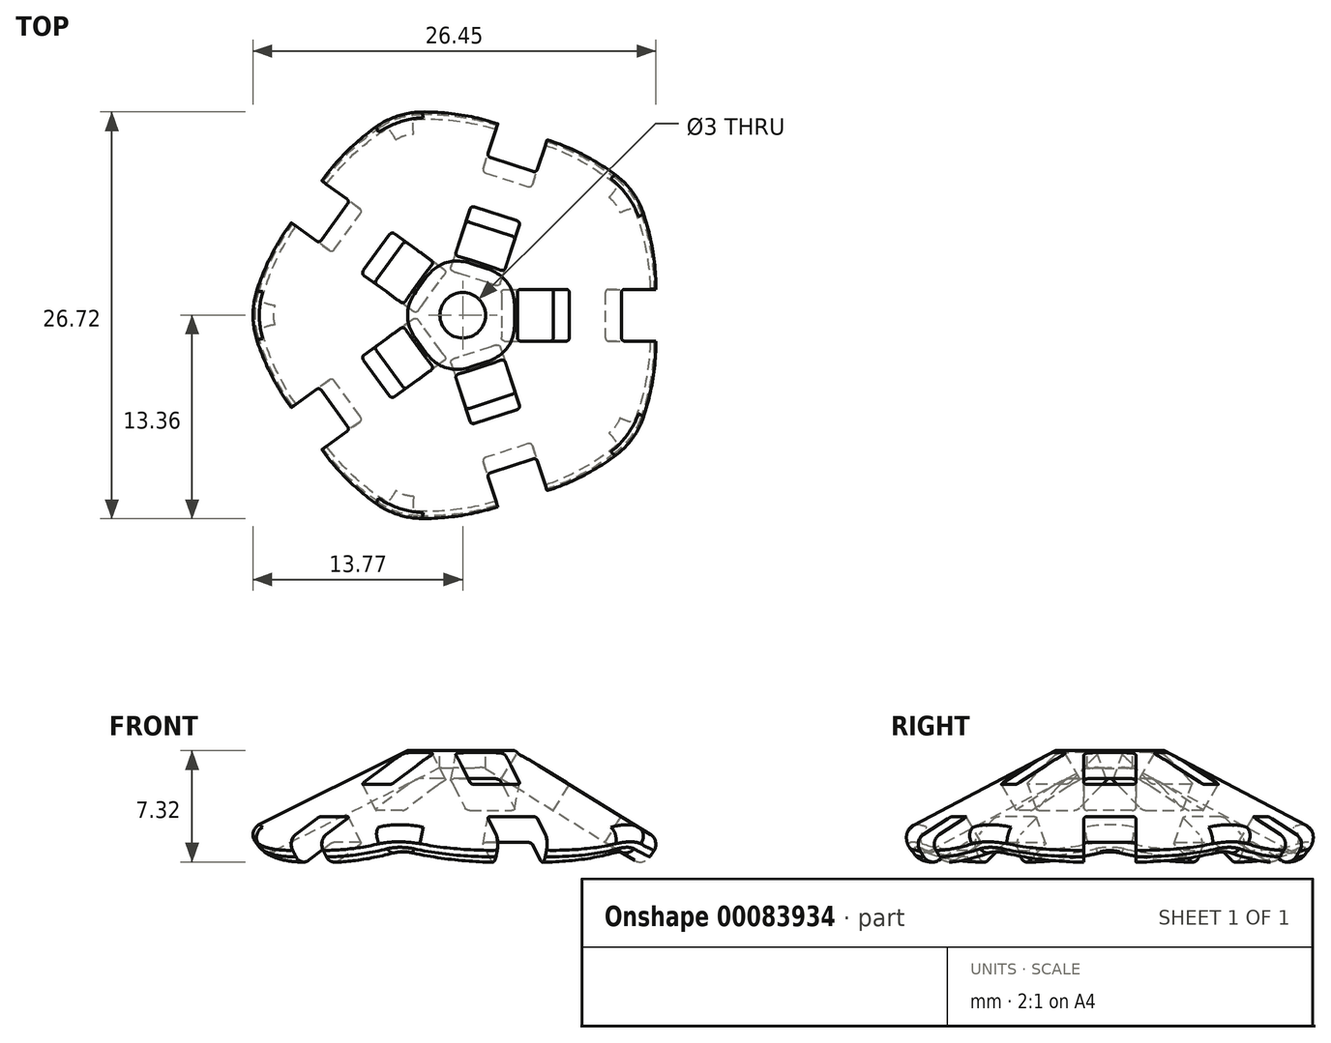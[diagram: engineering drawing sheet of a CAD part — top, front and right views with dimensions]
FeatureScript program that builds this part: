
annotation { "Feature Type Name" : "Feature", "Feature Type Description" : "" }
export const myFeature = defineFeature(function(context is Context, id is Id, definition is map)
    precondition{}
    {
        {
            var Q0;
            Q0=qCreatedBy(makeId("Front.planeOp"),FACE);
            var sketch = newSketch(context, id + "F0", { "sketchPlane" : qUnion([Q0])});
            skLineSegment(sketch, "E0", {"start": v(0, 0) * mm, "end": v(11.9, -7.36) * mm});
            skLineSegment(sketch, "E1.0", {"start": v(1.05, 1.7) * mm, "end": v(12.96, -5.66) * mm});
            skLineSegment(sketch, "E2", {"start": v(1.05, 1.7) * mm, "end": v(0, 0) * mm});
            skLineSegment(sketch, "E3", {"start": v(12.96, -5.66) * mm, "end": v(11.9, -7.36) * mm});
            skLineSegment(sketch, "E4", {"start": v(0, 0) * mm, "end": v(0, -18.92) * mm, "construction": true});
            skSolve(sketch);
        }
        {
            var Q0;
            Q0 = qSketchRegion(id + "F0", true);
            extrude(context, id + "F1", {"entities" : qUnion([Q0]), "endBound" : BoundingType.SYMMETRIC, "depth" : 20 * mm});
        }
        {
            var Q0;
            Q0=qCreatedBy(makeId("Top.planeOp"),FACE);
            var sketch = newSketch(context, id + "F2", { "sketchPlane" : qUnion([Q0])});
            skLineSegment(sketch, "E5", {"start": v(0, 0) * mm, "end": v(17.2, -12.5) * mm});
            skLineSegment(sketch, "E6", {"start": v(0, 0) * mm, "end": v(17.2, 12.5) * mm});
            skLineSegment(sketch, "E7", {"start": v(17.2, -12.5) * mm, "end": v(-2, -12.5) * mm});
            skLineSegment(sketch, "E8", {"start": v(-2, -12.5) * mm, "end": v(-2, 12.5) * mm});
            skLineSegment(sketch, "E9", {"start": v(-2, 12.5) * mm, "end": v(17.2, 12.5) * mm});
            skLineSegment(sketch, "E10", {"start": v(0, 0) * mm, "end": v(-2, 0) * mm});
            skLineSegment(sketch, "E11", {"start": v(17.2, -12.5) * mm, "end": v(17.2, 12.5) * mm});
            skSolve(sketch);
        }
        {
            var Q0;
            Q0=makeQuery(id+"F2.imprint","IMPRINT",FACE,{"disambiguationData":[TD([[makeQuery(id+"F2.imprint","IMPRINT",EDGE,{"derivedFrom":sQuery(id+"F2.wireOp",EDGE,"E6")}),1.0]])]});
            var Q1;
            Q1=makeQuery(id+"F2.imprint","IMPRINT",FACE,{"disambiguationData":[TD([[makeQuery(id+"F2.imprint","IMPRINT",EDGE,{"derivedFrom":sQuery(id+"F2.wireOp",EDGE,"E5")}),-1.0]])]});
            extrude(context, id + "F3", {"entities" : qUnion([Q0, Q1]), "operationType" : NewBodyOperationType.REMOVE, "endBound" : BoundingType.SYMMETRIC, "oppositeDirection" : true, "depth" : 25 * mm});
        }
        {
            var Q0;
            Q0=makeQuery(id+"F1.opExtrude","SWEPT_FACE",FACE,{"disambiguationData":[OSD([sQuery(id+"F0.wireOp",EDGE,"E1.0")])]});
            var sketch = newSketch(context, id + "F4", { "sketchPlane" : qUnion([Q0])});
            skLineSegment(sketch, "E12", {"start": v(0, 0) * mm, "end": v(14, 0) * mm, "construction": true});
            skLineSegment(sketch, "E13.bottom", {"start": v(11.25, -1.7) * mm, "end": v(15, -1.7) * mm});
            skLineSegment(sketch, "E13.top", {"start": v(11.25, 1.7) * mm, "end": v(15, 1.7) * mm});
            skLineSegment(sketch, "E13.left", {"start": v(11, -1.45) * mm, "end": v(11, 1.45) * mm});
            skPoint(sketch, "E13.middle", {"position": v(13, 0) * mm});
            skLineSegment(sketch, "E14.bottom", {"start": v(6.75, -1.7) * mm, "end": v(3.25, -1.7) * mm});
            skLineSegment(sketch, "E14.top", {"start": v(6.75, 1.7) * mm, "end": v(3.25, 1.7) * mm});
            skLineSegment(sketch, "E14.left", {"start": v(7, -1.45) * mm, "end": v(7, 1.45) * mm});
            skLineSegment(sketch, "E14.right", {"start": v(3, -1.45) * mm, "end": v(3, 1.45) * mm});
            skPoint(sketch, "E14.middle", {"position": v(5, 0) * mm});
            skPoint(sketch, "E15.visualSharp", {"position": v(3, -1.7) * mm});
            skArc(sketch, "E15.filletArc", {"start": v(3, -1.45) * mm, "mid": v(3.07, -1.63) * mm, "end": v(3.25, -1.7) * mm});
            skPoint(sketch, "E16.visualSharp", {"position": v(3, 1.7) * mm});
            skArc(sketch, "E16.filletArc", {"start": v(3.25, 1.7) * mm, "mid": v(3.07, 1.63) * mm, "end": v(3, 1.45) * mm});
            skPoint(sketch, "E17.visualSharp", {"position": v(7, -1.7) * mm});
            skArc(sketch, "E17.filletArc", {"start": v(6.75, -1.7) * mm, "mid": v(6.93, -1.63) * mm, "end": v(7, -1.45) * mm});
            skPoint(sketch, "E18.visualSharp", {"position": v(7, 1.7) * mm});
            skArc(sketch, "E18.filletArc", {"start": v(7, 1.45) * mm, "mid": v(6.93, 1.63) * mm, "end": v(6.75, 1.7) * mm});
            skPoint(sketch, "E19.visualSharp", {"position": v(11, 1.7) * mm});
            skArc(sketch, "E19.filletArc", {"start": v(11.25, 1.7) * mm, "mid": v(11.07, 1.63) * mm, "end": v(11, 1.45) * mm});
            skPoint(sketch, "E20.visualSharp", {"position": v(15, 1.7) * mm});
            skPoint(sketch, "E21.visualSharp", {"position": v(11, -1.7) * mm});
            skArc(sketch, "E21.filletArc", {"start": v(11, -1.45) * mm, "mid": v(11.07, -1.63) * mm, "end": v(11.25, -1.7) * mm});
            skPoint(sketch, "E22.visualSharp", {"position": v(15, -1.7) * mm});
            skLineSegment(sketch, "E23", {"start": v(15, -1.7) * mm, "end": v(15, 1.7) * mm});
            skSolve(sketch);
        }
        {
            var Q0;
            {var subQ0=sQuery(id+"F4.wireOp",EDGE,"E23");Q0=makeQuery(id+"F4.imprint","IMPRINT",FACE,{"disambiguationData":[TD([[makeQuery(id+"F4.imprint","IMPRINT",EDGE,{"derivedFrom":subQ0}),1.0]])]});}
            var Q1;
            Q1=makeQuery(id+"F4.imprint","IMPRINT",FACE,{"disambiguationData":[TD([[makeQuery(id+"F4.imprint","IMPRINT",EDGE,{"derivedFrom":sQuery(id+"F4.wireOp",EDGE,"E13.left")}),-1.0]])]});
            var Q2;
            {var subQ0=sQuery(id+"F4.wireOp",EDGE,"E23");Q2=makeQuery(id+"F4.imprint","IMPRINT",FACE,{"disambiguationData":[TD([[makeQuery(id+"F4.imprint","IMPRINT",EDGE,{"derivedFrom":subQ0}),1.0]])]});}
            var Q3;
            Q3=makeQuery(id+"F4.imprint","IMPRINT",FACE,{"disambiguationData":[TD([[makeQuery(id+"F4.imprint","IMPRINT",EDGE,{"derivedFrom":sQuery(id+"F4.wireOp",EDGE,"E14.bottom")}),-1.0]])]});
            extrude(context, id + "F5", {"entities" : qUnion([Q0, Q1, Q2, Q3]), "operationType" : NewBodyOperationType.REMOVE, "endBound" : BoundingType.UP_TO_NEXT, "oppositeDirection" : true, "depth" : 25 * mm});
        }
        {
            var Q0;
            Q0=qCreatedBy(makeId("Top.planeOp"),FACE);
            var sketch = newSketch(context, id + "F6", { "sketchPlane" : qUnion([Q0])});
            skCircle(sketch, "E24", {"center": v(0, 0) * mm, "radius": 2 * mm});
            skSolve(sketch);
        }
        {
            var Q0;
            Q0 = qSketchRegion(id + "F6", true);
            extrude(context, id + "F7", {"entities" : qUnion([Q0]), "operationType" : NewBodyOperationType.ADD, "depth" : 1.75 * mm});
        }
        {
            var Q0;
            Q0=makeQuery(id+"F1.opExtrude","SWEPT_BODY",BODY,{"disambiguationData":[OSD([sQuery(id+"F0.wireOp",EDGE,"E0"),sQuery(id+"F0.wireOp",EDGE,"E1.0"),sQuery(id+"F0.wireOp",EDGE,"E2"),sQuery(id+"F0.wireOp",EDGE,"E3")])]});
            var Q1;
            Q1=sQuery(id+"F0.wireOp",EDGE,"E4");
            circularPattern(context, id + "F8", {"operationType" : NewBodyOperationType.ADD, "entities" : qUnion([Q0]), "axis" : qUnion([Q1]), "angle" : 360 * degree, "instanceCount" : 5, "equalSpace" : true});
        }
        {
            var Q0;
            Q0=makeQuery(id+"F7.opExtrude","CAP_FACE",FACE,{"disambiguationData":[OSD([sQuery(id+"F6.wireOp",EDGE,"E24")])],"isStart":false});
            var sketch = newSketch(context, id + "F9", { "sketchPlane" : qUnion([Q0])});
            skCircle(sketch, "E25", {"center": v(0, 0) * mm, "radius": 1.5 * mm});
            skSolve(sketch);
        }
        {
            var Q0;
            Q0 = qSketchRegion(id + "F9", true);
            extrude(context, id + "F10", {"entities" : qUnion([Q0]), "operationType" : NewBodyOperationType.REMOVE, "oppositeDirection" : true, "depth" : 25 * mm});
        }
        {
            var Q0;
            {var subQ0=makeQuery(id+"F1.opExtrude","SWEPT_FACE",FACE,{"disambiguationData":[OSD([sQuery(id+"F0.wireOp",EDGE,"E1.0")])]});Q0=makeQuery(id+"F8.boolean.opBoolean","MERGE",EDGE,{"derivedFrom":[makeQuery(id+"F8.opPattern","COPY",EDGE,{"derivedFrom":makeQuery(id+"F3.boolean.opBoolean","INTERSECT",EDGE,{"derivedFrom":[subQ0,makeQuery(id+"F3.opExtrude","SWEPT_FACE",FACE,{"disambiguationData":[OSD([sQuery(id+"F2.wireOp",EDGE,"E5")])]})]}),"instanceName":"1"}),makeQuery(id+"F8.opPattern","COPY",EDGE,{"derivedFrom":makeQuery(id+"F3.boolean.opBoolean","INTERSECT",EDGE,{"derivedFrom":[subQ0,makeQuery(id+"F3.opExtrude","SWEPT_FACE",FACE,{"disambiguationData":[OSD([sQuery(id+"F2.wireOp",EDGE,"E6")])]})]}),"instanceName":"2"})]});}
            var Q1;
            {var subQ0=makeQuery(id+"F1.opExtrude","SWEPT_FACE",FACE,{"disambiguationData":[OSD([sQuery(id+"F0.wireOp",EDGE,"E1.0")])]});Q1=makeQuery(id+"F8.boolean.opBoolean","MERGE",EDGE,{"derivedFrom":[makeQuery(id+"F3.boolean.opBoolean","INTERSECT",EDGE,{"derivedFrom":[subQ0,makeQuery(id+"F3.opExtrude","SWEPT_FACE",FACE,{"disambiguationData":[OSD([sQuery(id+"F2.wireOp",EDGE,"E5")])]})]}),makeQuery(id+"F8.opPattern","COPY",EDGE,{"derivedFrom":makeQuery(id+"F3.boolean.opBoolean","INTERSECT",EDGE,{"derivedFrom":[subQ0,makeQuery(id+"F3.opExtrude","SWEPT_FACE",FACE,{"disambiguationData":[OSD([sQuery(id+"F2.wireOp",EDGE,"E6")])]})]}),"instanceName":"1"})]});}
            var Q2;
            {var subQ0=makeQuery(id+"F1.opExtrude","SWEPT_FACE",FACE,{"disambiguationData":[OSD([sQuery(id+"F0.wireOp",EDGE,"E1.0")])]});Q2=makeQuery(id+"F8.boolean.opBoolean","MERGE",EDGE,{"derivedFrom":[makeQuery(id+"F3.boolean.opBoolean","INTERSECT",EDGE,{"derivedFrom":[subQ0,makeQuery(id+"F3.opExtrude","SWEPT_FACE",FACE,{"disambiguationData":[OSD([sQuery(id+"F2.wireOp",EDGE,"E6")])]})]}),makeQuery(id+"F8.opPattern","COPY",EDGE,{"derivedFrom":makeQuery(id+"F3.boolean.opBoolean","INTERSECT",EDGE,{"derivedFrom":[subQ0,makeQuery(id+"F3.opExtrude","SWEPT_FACE",FACE,{"disambiguationData":[OSD([sQuery(id+"F2.wireOp",EDGE,"E5")])]})]}),"instanceName":"4"})]});}
            var Q3;
            {var subQ0=makeQuery(id+"F1.opExtrude","SWEPT_FACE",FACE,{"disambiguationData":[OSD([sQuery(id+"F0.wireOp",EDGE,"E1.0")])]});Q3=makeQuery(id+"F8.boolean.opBoolean","MERGE",EDGE,{"derivedFrom":[makeQuery(id+"F8.opPattern","COPY",EDGE,{"derivedFrom":makeQuery(id+"F3.boolean.opBoolean","INTERSECT",EDGE,{"derivedFrom":[subQ0,makeQuery(id+"F3.opExtrude","SWEPT_FACE",FACE,{"disambiguationData":[OSD([sQuery(id+"F2.wireOp",EDGE,"E5")])]})]}),"instanceName":"3"}),makeQuery(id+"F8.opPattern","COPY",EDGE,{"derivedFrom":makeQuery(id+"F3.boolean.opBoolean","INTERSECT",EDGE,{"derivedFrom":[subQ0,makeQuery(id+"F3.opExtrude","SWEPT_FACE",FACE,{"disambiguationData":[OSD([sQuery(id+"F2.wireOp",EDGE,"E6")])]})]}),"instanceName":"4"})]});}
            var Q4;
            {var subQ0=makeQuery(id+"F1.opExtrude","SWEPT_FACE",FACE,{"disambiguationData":[OSD([sQuery(id+"F0.wireOp",EDGE,"E1.0")])]});Q4=makeQuery(id+"F8.boolean.opBoolean","MERGE",EDGE,{"derivedFrom":[makeQuery(id+"F8.opPattern","COPY",EDGE,{"derivedFrom":makeQuery(id+"F3.boolean.opBoolean","INTERSECT",EDGE,{"derivedFrom":[subQ0,makeQuery(id+"F3.opExtrude","SWEPT_FACE",FACE,{"disambiguationData":[OSD([sQuery(id+"F2.wireOp",EDGE,"E5")])]})]}),"instanceName":"2"}),makeQuery(id+"F8.opPattern","COPY",EDGE,{"derivedFrom":makeQuery(id+"F3.boolean.opBoolean","INTERSECT",EDGE,{"derivedFrom":[subQ0,makeQuery(id+"F3.opExtrude","SWEPT_FACE",FACE,{"disambiguationData":[OSD([sQuery(id+"F2.wireOp",EDGE,"E6")])]})]}),"instanceName":"3"})]});}
            fillet(context, id + "F11", {"entities" : qUnion([Q0, Q1, Q2, Q3, Q4]), "radius" : 5 * mm, "tangentPropagation" : true, "allowEdgeOverflow" : false});
        }
        {
            var Q0;
            {var subQ0=makeQuery(id+"F1.opExtrude","SWEPT_FACE",FACE,{"disambiguationData":[OSD([sQuery(id+"F0.wireOp",EDGE,"E3")])]});Q0=makeQuery(id+"F8.boolean.opBoolean","MERGE",EDGE,{"derivedFrom":[makeQuery(id+"F3.boolean.opBoolean","INTERSECT",EDGE,{"derivedFrom":[subQ0,makeQuery(id+"F3.opExtrude","SWEPT_FACE",FACE,{"disambiguationData":[OSD([sQuery(id+"F2.wireOp",EDGE,"E5")])]})]}),makeQuery(id+"F8.opPattern","COPY",EDGE,{"derivedFrom":makeQuery(id+"F3.boolean.opBoolean","INTERSECT",EDGE,{"derivedFrom":[subQ0,makeQuery(id+"F3.opExtrude","SWEPT_FACE",FACE,{"disambiguationData":[OSD([sQuery(id+"F2.wireOp",EDGE,"E6")])]})]}),"instanceName":"1"})]});}
            var Q1;
            {var subQ0=makeQuery(id+"F1.opExtrude","SWEPT_FACE",FACE,{"disambiguationData":[OSD([sQuery(id+"F0.wireOp",EDGE,"E3")])]});Q1=makeQuery(id+"F8.boolean.opBoolean","MERGE",EDGE,{"derivedFrom":[makeQuery(id+"F3.boolean.opBoolean","INTERSECT",EDGE,{"derivedFrom":[subQ0,makeQuery(id+"F3.opExtrude","SWEPT_FACE",FACE,{"disambiguationData":[OSD([sQuery(id+"F2.wireOp",EDGE,"E6")])]})]}),makeQuery(id+"F8.opPattern","COPY",EDGE,{"derivedFrom":makeQuery(id+"F3.boolean.opBoolean","INTERSECT",EDGE,{"derivedFrom":[subQ0,makeQuery(id+"F3.opExtrude","SWEPT_FACE",FACE,{"disambiguationData":[OSD([sQuery(id+"F2.wireOp",EDGE,"E5")])]})]}),"instanceName":"4"})]});}
            var Q2;
            {var subQ0=makeQuery(id+"F1.opExtrude","SWEPT_FACE",FACE,{"disambiguationData":[OSD([sQuery(id+"F0.wireOp",EDGE,"E3")])]});Q2=makeQuery(id+"F8.boolean.opBoolean","MERGE",EDGE,{"derivedFrom":[makeQuery(id+"F8.opPattern","COPY",EDGE,{"derivedFrom":makeQuery(id+"F3.boolean.opBoolean","INTERSECT",EDGE,{"derivedFrom":[subQ0,makeQuery(id+"F3.opExtrude","SWEPT_FACE",FACE,{"disambiguationData":[OSD([sQuery(id+"F2.wireOp",EDGE,"E5")])]})]}),"instanceName":"3"}),makeQuery(id+"F8.opPattern","COPY",EDGE,{"derivedFrom":makeQuery(id+"F3.boolean.opBoolean","INTERSECT",EDGE,{"derivedFrom":[subQ0,makeQuery(id+"F3.opExtrude","SWEPT_FACE",FACE,{"disambiguationData":[OSD([sQuery(id+"F2.wireOp",EDGE,"E6")])]})]}),"instanceName":"4"})]});}
            var Q3;
            {var subQ0=makeQuery(id+"F1.opExtrude","SWEPT_FACE",FACE,{"disambiguationData":[OSD([sQuery(id+"F0.wireOp",EDGE,"E3")])]});Q3=makeQuery(id+"F8.boolean.opBoolean","MERGE",EDGE,{"derivedFrom":[makeQuery(id+"F8.opPattern","COPY",EDGE,{"derivedFrom":makeQuery(id+"F3.boolean.opBoolean","INTERSECT",EDGE,{"derivedFrom":[subQ0,makeQuery(id+"F3.opExtrude","SWEPT_FACE",FACE,{"disambiguationData":[OSD([sQuery(id+"F2.wireOp",EDGE,"E5")])]})]}),"instanceName":"2"}),makeQuery(id+"F8.opPattern","COPY",EDGE,{"derivedFrom":makeQuery(id+"F3.boolean.opBoolean","INTERSECT",EDGE,{"derivedFrom":[subQ0,makeQuery(id+"F3.opExtrude","SWEPT_FACE",FACE,{"disambiguationData":[OSD([sQuery(id+"F2.wireOp",EDGE,"E6")])]})]}),"instanceName":"3"})]});}
            var Q4;
            {var subQ0=makeQuery(id+"F1.opExtrude","SWEPT_FACE",FACE,{"disambiguationData":[OSD([sQuery(id+"F0.wireOp",EDGE,"E3")])]});Q4=makeQuery(id+"F8.boolean.opBoolean","MERGE",EDGE,{"derivedFrom":[makeQuery(id+"F8.opPattern","COPY",EDGE,{"derivedFrom":makeQuery(id+"F3.boolean.opBoolean","INTERSECT",EDGE,{"derivedFrom":[subQ0,makeQuery(id+"F3.opExtrude","SWEPT_FACE",FACE,{"disambiguationData":[OSD([sQuery(id+"F2.wireOp",EDGE,"E5")])]})]}),"instanceName":"1"}),makeQuery(id+"F8.opPattern","COPY",EDGE,{"derivedFrom":makeQuery(id+"F3.boolean.opBoolean","INTERSECT",EDGE,{"derivedFrom":[subQ0,makeQuery(id+"F3.opExtrude","SWEPT_FACE",FACE,{"disambiguationData":[OSD([sQuery(id+"F2.wireOp",EDGE,"E6")])]})]}),"instanceName":"2"})]});}
            fillet(context, id + "F12", {"entities" : qUnion([Q0, Q1, Q2, Q3, Q4]), "radius" : 12 * mm, "tangentPropagation" : true, "allowEdgeOverflow" : false});
        }
        {
            var Q0;
            {var subQ0=makeQuery(id+"F1.opExtrude","SWEPT_FACE",FACE,{"disambiguationData":[OSD([sQuery(id+"F0.wireOp",EDGE,"E0")])]});Q0=makeQuery(id+"F8.boolean.opBoolean","MERGE",EDGE,{"derivedFrom":[makeQuery(id+"F8.opPattern","COPY",EDGE,{"derivedFrom":makeQuery(id+"F3.boolean.opBoolean","INTERSECT",EDGE,{"derivedFrom":[subQ0,makeQuery(id+"F3.opExtrude","SWEPT_FACE",FACE,{"disambiguationData":[OSD([sQuery(id+"F2.wireOp",EDGE,"E5")])]})]}),"instanceName":"1"}),makeQuery(id+"F8.opPattern","COPY",EDGE,{"derivedFrom":makeQuery(id+"F3.boolean.opBoolean","INTERSECT",EDGE,{"derivedFrom":[subQ0,makeQuery(id+"F3.opExtrude","SWEPT_FACE",FACE,{"disambiguationData":[OSD([sQuery(id+"F2.wireOp",EDGE,"E6")])]})]}),"instanceName":"2"})]});}
            var Q1;
            {var subQ0=makeQuery(id+"F1.opExtrude","SWEPT_FACE",FACE,{"disambiguationData":[OSD([sQuery(id+"F0.wireOp",EDGE,"E0")])]});Q1=makeQuery(id+"F8.boolean.opBoolean","MERGE",EDGE,{"derivedFrom":[makeQuery(id+"F8.opPattern","COPY",EDGE,{"derivedFrom":makeQuery(id+"F3.boolean.opBoolean","INTERSECT",EDGE,{"derivedFrom":[subQ0,makeQuery(id+"F3.opExtrude","SWEPT_FACE",FACE,{"disambiguationData":[OSD([sQuery(id+"F2.wireOp",EDGE,"E5")])]})]}),"instanceName":"2"}),makeQuery(id+"F8.opPattern","COPY",EDGE,{"derivedFrom":makeQuery(id+"F3.boolean.opBoolean","INTERSECT",EDGE,{"derivedFrom":[subQ0,makeQuery(id+"F3.opExtrude","SWEPT_FACE",FACE,{"disambiguationData":[OSD([sQuery(id+"F2.wireOp",EDGE,"E6")])]})]}),"instanceName":"3"})]});}
            var Q2;
            {var subQ0=makeQuery(id+"F1.opExtrude","SWEPT_FACE",FACE,{"disambiguationData":[OSD([sQuery(id+"F0.wireOp",EDGE,"E0")])]});Q2=makeQuery(id+"F8.boolean.opBoolean","MERGE",EDGE,{"derivedFrom":[makeQuery(id+"F8.opPattern","COPY",EDGE,{"derivedFrom":makeQuery(id+"F3.boolean.opBoolean","INTERSECT",EDGE,{"derivedFrom":[subQ0,makeQuery(id+"F3.opExtrude","SWEPT_FACE",FACE,{"disambiguationData":[OSD([sQuery(id+"F2.wireOp",EDGE,"E5")])]})]}),"instanceName":"3"}),makeQuery(id+"F8.opPattern","COPY",EDGE,{"derivedFrom":makeQuery(id+"F3.boolean.opBoolean","INTERSECT",EDGE,{"derivedFrom":[subQ0,makeQuery(id+"F3.opExtrude","SWEPT_FACE",FACE,{"disambiguationData":[OSD([sQuery(id+"F2.wireOp",EDGE,"E6")])]})]}),"instanceName":"4"})]});}
            var Q3;
            {var subQ0=makeQuery(id+"F1.opExtrude","SWEPT_FACE",FACE,{"disambiguationData":[OSD([sQuery(id+"F0.wireOp",EDGE,"E0")])]});Q3=makeQuery(id+"F8.boolean.opBoolean","MERGE",EDGE,{"derivedFrom":[makeQuery(id+"F3.boolean.opBoolean","INTERSECT",EDGE,{"derivedFrom":[subQ0,makeQuery(id+"F3.opExtrude","SWEPT_FACE",FACE,{"disambiguationData":[OSD([sQuery(id+"F2.wireOp",EDGE,"E6")])]})]}),makeQuery(id+"F8.opPattern","COPY",EDGE,{"derivedFrom":makeQuery(id+"F3.boolean.opBoolean","INTERSECT",EDGE,{"derivedFrom":[subQ0,makeQuery(id+"F3.opExtrude","SWEPT_FACE",FACE,{"disambiguationData":[OSD([sQuery(id+"F2.wireOp",EDGE,"E5")])]})]}),"instanceName":"4"})]});}
            var Q4;
            {var subQ0=makeQuery(id+"F1.opExtrude","SWEPT_FACE",FACE,{"disambiguationData":[OSD([sQuery(id+"F0.wireOp",EDGE,"E0")])]});Q4=makeQuery(id+"F8.boolean.opBoolean","MERGE",EDGE,{"derivedFrom":[makeQuery(id+"F3.boolean.opBoolean","INTERSECT",EDGE,{"derivedFrom":[subQ0,makeQuery(id+"F3.opExtrude","SWEPT_FACE",FACE,{"disambiguationData":[OSD([sQuery(id+"F2.wireOp",EDGE,"E5")])]})]}),makeQuery(id+"F8.opPattern","COPY",EDGE,{"derivedFrom":makeQuery(id+"F3.boolean.opBoolean","INTERSECT",EDGE,{"derivedFrom":[subQ0,makeQuery(id+"F3.opExtrude","SWEPT_FACE",FACE,{"disambiguationData":[OSD([sQuery(id+"F2.wireOp",EDGE,"E6")])]})]}),"instanceName":"1"})]});}
            fillet(context, id + "F13", {"entities" : qUnion([Q0, Q1, Q2, Q3, Q4]), "radius" : 2 * mm, "tangentPropagation" : true, "allowEdgeOverflow" : false});
        }
        {
            var Q0;
            {var subQ0=sQuery(id+"F2.wireOp",EDGE,"E5");var subQ1=makeQuery(id+"F3.opExtrude","SWEPT_FACE",FACE,{"disambiguationData":[OSD([subQ0])]});var subQ2=sQuery(id+"F0.wireOp",EDGE,"E1.0");var subQ3=makeQuery(id+"F1.opExtrude","SWEPT_FACE",FACE,{"disambiguationData":[OSD([subQ2])]});var subQ4=sQuery(id+"F2.wireOp",EDGE,"E6");var subQ5=makeQuery(id+"F3.opExtrude","SWEPT_FACE",FACE,{"disambiguationData":[OSD([subQ4])]});var subQ6=makeQuery(id+"F1.opExtrude","SWEPT_FACE",FACE,{"disambiguationData":[OSD([sQuery(id+"F0.wireOp",EDGE,"E3")])]});Q0=makeQuery(id+"F12.opFillet","BLEND_EDGE",EDGE,{"blendedFrom":[makeQuery(id+"F8.boolean.opBoolean","MERGE",EDGE,{"derivedFrom":[makeQuery(id+"F3.boolean.opBoolean","INTERSECT",EDGE,{"derivedFrom":[subQ6,subQ5]}),makeQuery(id+"F8.opPattern","COPY",EDGE,{"derivedFrom":makeQuery(id+"F3.boolean.opBoolean","INTERSECT",EDGE,{"derivedFrom":[subQ6,subQ1]}),"instanceName":"4"})]}),makeQuery(id+"F11.opFillet","BLEND_FACE",FACE,{"disambiguationData":[OSD([subQ2,subQ0,subQ4]),TDD([makeQuery(id+"F8.boolean.opBoolean","MERGE",EDGE,{"derivedFrom":[makeQuery(id+"F3.boolean.opBoolean","INTERSECT",EDGE,{"derivedFrom":[subQ3,subQ5]}),makeQuery(id+"F8.opPattern","COPY",EDGE,{"derivedFrom":makeQuery(id+"F3.boolean.opBoolean","INTERSECT",EDGE,{"derivedFrom":[subQ3,subQ1]}),"instanceName":"4"})]})])]})],"blendedInto":[makeQuery(id+"F11.opFillet","BLEND_FACE",FACE,{"disambiguationData":[OSD([subQ2,subQ0,subQ4]),TDD([makeQuery(id+"F8.boolean.opBoolean","MERGE",EDGE,{"derivedFrom":[makeQuery(id+"F3.boolean.opBoolean","INTERSECT",EDGE,{"derivedFrom":[subQ3,subQ5]}),makeQuery(id+"F8.opPattern","COPY",EDGE,{"derivedFrom":makeQuery(id+"F3.boolean.opBoolean","INTERSECT",EDGE,{"derivedFrom":[subQ3,subQ1]}),"instanceName":"4"})]})])]})]});}
            var Q1;
            {var subQ0=sQuery(id+"F2.wireOp",EDGE,"E5");var subQ1=makeQuery(id+"F3.opExtrude","SWEPT_FACE",FACE,{"disambiguationData":[OSD([subQ0])]});var subQ2=sQuery(id+"F0.wireOp",EDGE,"E3");var subQ3=makeQuery(id+"F1.opExtrude","SWEPT_FACE",FACE,{"disambiguationData":[OSD([subQ2])]});var subQ4=sQuery(id+"F2.wireOp",EDGE,"E6");var subQ5=makeQuery(id+"F3.opExtrude","SWEPT_FACE",FACE,{"disambiguationData":[OSD([subQ4])]});var subQ6=makeQuery(id+"F1.opExtrude","SWEPT_FACE",FACE,{"disambiguationData":[OSD([sQuery(id+"F0.wireOp",EDGE,"E0")])]});Q1=makeQuery(id+"F13.opFillet","BLEND_EDGE",EDGE,{"blendedFrom":[makeQuery(id+"F8.boolean.opBoolean","MERGE",EDGE,{"derivedFrom":[makeQuery(id+"F3.boolean.opBoolean","INTERSECT",EDGE,{"derivedFrom":[subQ6,subQ5]}),makeQuery(id+"F8.opPattern","COPY",EDGE,{"derivedFrom":makeQuery(id+"F3.boolean.opBoolean","INTERSECT",EDGE,{"derivedFrom":[subQ6,subQ1]}),"instanceName":"4"})]}),makeQuery(id+"F12.opFillet","BLEND_FACE",FACE,{"disambiguationData":[OSD([subQ2,subQ0,subQ4]),TDD([makeQuery(id+"F8.boolean.opBoolean","MERGE",EDGE,{"derivedFrom":[makeQuery(id+"F3.boolean.opBoolean","INTERSECT",EDGE,{"derivedFrom":[subQ3,subQ5]}),makeQuery(id+"F8.opPattern","COPY",EDGE,{"derivedFrom":makeQuery(id+"F3.boolean.opBoolean","INTERSECT",EDGE,{"derivedFrom":[subQ3,subQ1]}),"instanceName":"4"})]})])]})],"blendedInto":[makeQuery(id+"F12.opFillet","BLEND_FACE",FACE,{"disambiguationData":[OSD([subQ2,subQ0,subQ4]),TDD([makeQuery(id+"F8.boolean.opBoolean","MERGE",EDGE,{"derivedFrom":[makeQuery(id+"F3.boolean.opBoolean","INTERSECT",EDGE,{"derivedFrom":[subQ3,subQ5]}),makeQuery(id+"F8.opPattern","COPY",EDGE,{"derivedFrom":makeQuery(id+"F3.boolean.opBoolean","INTERSECT",EDGE,{"derivedFrom":[subQ3,subQ1]}),"instanceName":"4"})]})])]})]});}
            var Q2;
            {var subQ0=sQuery(id+"F2.wireOp",EDGE,"E6");var subQ1=makeQuery(id+"F3.opExtrude","SWEPT_FACE",FACE,{"disambiguationData":[OSD([subQ0])]});var subQ2=sQuery(id+"F0.wireOp",EDGE,"E1.0");var subQ3=makeQuery(id+"F1.opExtrude","SWEPT_FACE",FACE,{"disambiguationData":[OSD([subQ2])]});var subQ4=sQuery(id+"F2.wireOp",EDGE,"E5");var subQ5=makeQuery(id+"F3.opExtrude","SWEPT_FACE",FACE,{"disambiguationData":[OSD([subQ4])]});var subQ6=makeQuery(id+"F1.opExtrude","SWEPT_FACE",FACE,{"disambiguationData":[OSD([sQuery(id+"F0.wireOp",EDGE,"E3")])]});Q2=makeQuery(id+"F12.opFillet","BLEND_EDGE",EDGE,{"blendedFrom":[makeQuery(id+"F8.boolean.opBoolean","MERGE",EDGE,{"derivedFrom":[makeQuery(id+"F3.boolean.opBoolean","INTERSECT",EDGE,{"derivedFrom":[subQ6,subQ5]}),makeQuery(id+"F8.opPattern","COPY",EDGE,{"derivedFrom":makeQuery(id+"F3.boolean.opBoolean","INTERSECT",EDGE,{"derivedFrom":[subQ6,subQ1]}),"instanceName":"1"})]}),makeQuery(id+"F11.opFillet","BLEND_FACE",FACE,{"disambiguationData":[OSD([subQ2,subQ4,subQ0]),TDD([makeQuery(id+"F8.boolean.opBoolean","MERGE",EDGE,{"derivedFrom":[makeQuery(id+"F3.boolean.opBoolean","INTERSECT",EDGE,{"derivedFrom":[subQ3,subQ5]}),makeQuery(id+"F8.opPattern","COPY",EDGE,{"derivedFrom":makeQuery(id+"F3.boolean.opBoolean","INTERSECT",EDGE,{"derivedFrom":[subQ3,subQ1]}),"instanceName":"1"})]})])]})],"blendedInto":[makeQuery(id+"F11.opFillet","BLEND_FACE",FACE,{"disambiguationData":[OSD([subQ2,subQ4,subQ0]),TDD([makeQuery(id+"F8.boolean.opBoolean","MERGE",EDGE,{"derivedFrom":[makeQuery(id+"F3.boolean.opBoolean","INTERSECT",EDGE,{"derivedFrom":[subQ3,subQ5]}),makeQuery(id+"F8.opPattern","COPY",EDGE,{"derivedFrom":makeQuery(id+"F3.boolean.opBoolean","INTERSECT",EDGE,{"derivedFrom":[subQ3,subQ1]}),"instanceName":"1"})]})])]})]});}
            var Q3;
            {var subQ0=sQuery(id+"F2.wireOp",EDGE,"E6");var subQ1=makeQuery(id+"F3.opExtrude","SWEPT_FACE",FACE,{"disambiguationData":[OSD([subQ0])]});var subQ2=sQuery(id+"F0.wireOp",EDGE,"E3");var subQ3=makeQuery(id+"F1.opExtrude","SWEPT_FACE",FACE,{"disambiguationData":[OSD([subQ2])]});var subQ4=sQuery(id+"F2.wireOp",EDGE,"E5");var subQ5=makeQuery(id+"F3.opExtrude","SWEPT_FACE",FACE,{"disambiguationData":[OSD([subQ4])]});var subQ6=makeQuery(id+"F1.opExtrude","SWEPT_FACE",FACE,{"disambiguationData":[OSD([sQuery(id+"F0.wireOp",EDGE,"E0")])]});Q3=makeQuery(id+"F13.opFillet","BLEND_EDGE",EDGE,{"blendedFrom":[makeQuery(id+"F8.boolean.opBoolean","MERGE",EDGE,{"derivedFrom":[makeQuery(id+"F3.boolean.opBoolean","INTERSECT",EDGE,{"derivedFrom":[subQ6,subQ5]}),makeQuery(id+"F8.opPattern","COPY",EDGE,{"derivedFrom":makeQuery(id+"F3.boolean.opBoolean","INTERSECT",EDGE,{"derivedFrom":[subQ6,subQ1]}),"instanceName":"1"})]}),makeQuery(id+"F12.opFillet","BLEND_FACE",FACE,{"disambiguationData":[OSD([subQ2,subQ4,subQ0]),TDD([makeQuery(id+"F8.boolean.opBoolean","MERGE",EDGE,{"derivedFrom":[makeQuery(id+"F3.boolean.opBoolean","INTERSECT",EDGE,{"derivedFrom":[subQ3,subQ5]}),makeQuery(id+"F8.opPattern","COPY",EDGE,{"derivedFrom":makeQuery(id+"F3.boolean.opBoolean","INTERSECT",EDGE,{"derivedFrom":[subQ3,subQ1]}),"instanceName":"1"})]})])]})],"blendedInto":[makeQuery(id+"F12.opFillet","BLEND_FACE",FACE,{"disambiguationData":[OSD([subQ2,subQ4,subQ0]),TDD([makeQuery(id+"F8.boolean.opBoolean","MERGE",EDGE,{"derivedFrom":[makeQuery(id+"F3.boolean.opBoolean","INTERSECT",EDGE,{"derivedFrom":[subQ3,subQ5]}),makeQuery(id+"F8.opPattern","COPY",EDGE,{"derivedFrom":makeQuery(id+"F3.boolean.opBoolean","INTERSECT",EDGE,{"derivedFrom":[subQ3,subQ1]}),"instanceName":"1"})]})])]})]});}
            var Q4;
            {var subQ0=sQuery(id+"F2.wireOp",EDGE,"E6");var subQ1=makeQuery(id+"F3.opExtrude","SWEPT_FACE",FACE,{"disambiguationData":[OSD([subQ0])]});var subQ2=sQuery(id+"F0.wireOp",EDGE,"E1.0");var subQ3=makeQuery(id+"F1.opExtrude","SWEPT_FACE",FACE,{"disambiguationData":[OSD([subQ2])]});var subQ4=sQuery(id+"F2.wireOp",EDGE,"E5");var subQ5=makeQuery(id+"F3.opExtrude","SWEPT_FACE",FACE,{"disambiguationData":[OSD([subQ4])]});var subQ6=makeQuery(id+"F1.opExtrude","SWEPT_FACE",FACE,{"disambiguationData":[OSD([sQuery(id+"F0.wireOp",EDGE,"E3")])]});Q4=makeQuery(id+"F12.opFillet","BLEND_EDGE",EDGE,{"blendedFrom":[makeQuery(id+"F8.boolean.opBoolean","MERGE",EDGE,{"derivedFrom":[makeQuery(id+"F8.opPattern","COPY",EDGE,{"derivedFrom":makeQuery(id+"F3.boolean.opBoolean","INTERSECT",EDGE,{"derivedFrom":[subQ6,subQ5]}),"instanceName":"1"}),makeQuery(id+"F8.opPattern","COPY",EDGE,{"derivedFrom":makeQuery(id+"F3.boolean.opBoolean","INTERSECT",EDGE,{"derivedFrom":[subQ6,subQ1]}),"instanceName":"2"})]}),makeQuery(id+"F11.opFillet","BLEND_FACE",FACE,{"disambiguationData":[OSD([subQ2,subQ4,subQ0]),TDD([makeQuery(id+"F8.boolean.opBoolean","MERGE",EDGE,{"derivedFrom":[makeQuery(id+"F8.opPattern","COPY",EDGE,{"derivedFrom":makeQuery(id+"F3.boolean.opBoolean","INTERSECT",EDGE,{"derivedFrom":[subQ3,subQ5]}),"instanceName":"1"}),makeQuery(id+"F8.opPattern","COPY",EDGE,{"derivedFrom":makeQuery(id+"F3.boolean.opBoolean","INTERSECT",EDGE,{"derivedFrom":[subQ3,subQ1]}),"instanceName":"2"})]})])]})],"blendedInto":[makeQuery(id+"F11.opFillet","BLEND_FACE",FACE,{"disambiguationData":[OSD([subQ2,subQ4,subQ0]),TDD([makeQuery(id+"F8.boolean.opBoolean","MERGE",EDGE,{"derivedFrom":[makeQuery(id+"F8.opPattern","COPY",EDGE,{"derivedFrom":makeQuery(id+"F3.boolean.opBoolean","INTERSECT",EDGE,{"derivedFrom":[subQ3,subQ5]}),"instanceName":"1"}),makeQuery(id+"F8.opPattern","COPY",EDGE,{"derivedFrom":makeQuery(id+"F3.boolean.opBoolean","INTERSECT",EDGE,{"derivedFrom":[subQ3,subQ1]}),"instanceName":"2"})]})])]})]});}
            var Q5;
            {var subQ0=sQuery(id+"F2.wireOp",EDGE,"E6");var subQ1=makeQuery(id+"F3.opExtrude","SWEPT_FACE",FACE,{"disambiguationData":[OSD([subQ0])]});var subQ2=sQuery(id+"F0.wireOp",EDGE,"E3");var subQ3=makeQuery(id+"F1.opExtrude","SWEPT_FACE",FACE,{"disambiguationData":[OSD([subQ2])]});var subQ4=sQuery(id+"F2.wireOp",EDGE,"E5");var subQ5=makeQuery(id+"F3.opExtrude","SWEPT_FACE",FACE,{"disambiguationData":[OSD([subQ4])]});var subQ6=makeQuery(id+"F1.opExtrude","SWEPT_FACE",FACE,{"disambiguationData":[OSD([sQuery(id+"F0.wireOp",EDGE,"E0")])]});Q5=makeQuery(id+"F13.opFillet","BLEND_EDGE",EDGE,{"blendedFrom":[makeQuery(id+"F8.boolean.opBoolean","MERGE",EDGE,{"derivedFrom":[makeQuery(id+"F8.opPattern","COPY",EDGE,{"derivedFrom":makeQuery(id+"F3.boolean.opBoolean","INTERSECT",EDGE,{"derivedFrom":[subQ6,subQ5]}),"instanceName":"1"}),makeQuery(id+"F8.opPattern","COPY",EDGE,{"derivedFrom":makeQuery(id+"F3.boolean.opBoolean","INTERSECT",EDGE,{"derivedFrom":[subQ6,subQ1]}),"instanceName":"2"})]}),makeQuery(id+"F12.opFillet","BLEND_FACE",FACE,{"disambiguationData":[OSD([subQ2,subQ4,subQ0]),TDD([makeQuery(id+"F8.boolean.opBoolean","MERGE",EDGE,{"derivedFrom":[makeQuery(id+"F8.opPattern","COPY",EDGE,{"derivedFrom":makeQuery(id+"F3.boolean.opBoolean","INTERSECT",EDGE,{"derivedFrom":[subQ3,subQ5]}),"instanceName":"1"}),makeQuery(id+"F8.opPattern","COPY",EDGE,{"derivedFrom":makeQuery(id+"F3.boolean.opBoolean","INTERSECT",EDGE,{"derivedFrom":[subQ3,subQ1]}),"instanceName":"2"})]})])]})],"blendedInto":[makeQuery(id+"F12.opFillet","BLEND_FACE",FACE,{"disambiguationData":[OSD([subQ2,subQ4,subQ0]),TDD([makeQuery(id+"F8.boolean.opBoolean","MERGE",EDGE,{"derivedFrom":[makeQuery(id+"F8.opPattern","COPY",EDGE,{"derivedFrom":makeQuery(id+"F3.boolean.opBoolean","INTERSECT",EDGE,{"derivedFrom":[subQ3,subQ5]}),"instanceName":"1"}),makeQuery(id+"F8.opPattern","COPY",EDGE,{"derivedFrom":makeQuery(id+"F3.boolean.opBoolean","INTERSECT",EDGE,{"derivedFrom":[subQ3,subQ1]}),"instanceName":"2"})]})])]})]});}
            var Q6;
            {var subQ0=sQuery(id+"F2.wireOp",EDGE,"E6");var subQ1=makeQuery(id+"F3.opExtrude","SWEPT_FACE",FACE,{"disambiguationData":[OSD([subQ0])]});var subQ2=sQuery(id+"F0.wireOp",EDGE,"E1.0");var subQ3=makeQuery(id+"F1.opExtrude","SWEPT_FACE",FACE,{"disambiguationData":[OSD([subQ2])]});var subQ4=sQuery(id+"F2.wireOp",EDGE,"E5");var subQ5=makeQuery(id+"F3.opExtrude","SWEPT_FACE",FACE,{"disambiguationData":[OSD([subQ4])]});var subQ6=makeQuery(id+"F1.opExtrude","SWEPT_FACE",FACE,{"disambiguationData":[OSD([sQuery(id+"F0.wireOp",EDGE,"E3")])]});Q6=makeQuery(id+"F12.opFillet","BLEND_EDGE",EDGE,{"blendedFrom":[makeQuery(id+"F8.boolean.opBoolean","MERGE",EDGE,{"derivedFrom":[makeQuery(id+"F8.opPattern","COPY",EDGE,{"derivedFrom":makeQuery(id+"F3.boolean.opBoolean","INTERSECT",EDGE,{"derivedFrom":[subQ6,subQ5]}),"instanceName":"2"}),makeQuery(id+"F8.opPattern","COPY",EDGE,{"derivedFrom":makeQuery(id+"F3.boolean.opBoolean","INTERSECT",EDGE,{"derivedFrom":[subQ6,subQ1]}),"instanceName":"3"})]}),makeQuery(id+"F11.opFillet","BLEND_FACE",FACE,{"disambiguationData":[OSD([subQ2,subQ4,subQ0]),TDD([makeQuery(id+"F8.boolean.opBoolean","MERGE",EDGE,{"derivedFrom":[makeQuery(id+"F8.opPattern","COPY",EDGE,{"derivedFrom":makeQuery(id+"F3.boolean.opBoolean","INTERSECT",EDGE,{"derivedFrom":[subQ3,subQ5]}),"instanceName":"2"}),makeQuery(id+"F8.opPattern","COPY",EDGE,{"derivedFrom":makeQuery(id+"F3.boolean.opBoolean","INTERSECT",EDGE,{"derivedFrom":[subQ3,subQ1]}),"instanceName":"3"})]})])]})],"blendedInto":[makeQuery(id+"F11.opFillet","BLEND_FACE",FACE,{"disambiguationData":[OSD([subQ2,subQ4,subQ0]),TDD([makeQuery(id+"F8.boolean.opBoolean","MERGE",EDGE,{"derivedFrom":[makeQuery(id+"F8.opPattern","COPY",EDGE,{"derivedFrom":makeQuery(id+"F3.boolean.opBoolean","INTERSECT",EDGE,{"derivedFrom":[subQ3,subQ5]}),"instanceName":"2"}),makeQuery(id+"F8.opPattern","COPY",EDGE,{"derivedFrom":makeQuery(id+"F3.boolean.opBoolean","INTERSECT",EDGE,{"derivedFrom":[subQ3,subQ1]}),"instanceName":"3"})]})])]})]});}
            var Q7;
            {var subQ0=sQuery(id+"F2.wireOp",EDGE,"E6");var subQ1=makeQuery(id+"F3.opExtrude","SWEPT_FACE",FACE,{"disambiguationData":[OSD([subQ0])]});var subQ2=sQuery(id+"F0.wireOp",EDGE,"E3");var subQ3=makeQuery(id+"F1.opExtrude","SWEPT_FACE",FACE,{"disambiguationData":[OSD([subQ2])]});var subQ4=sQuery(id+"F2.wireOp",EDGE,"E5");var subQ5=makeQuery(id+"F3.opExtrude","SWEPT_FACE",FACE,{"disambiguationData":[OSD([subQ4])]});var subQ6=makeQuery(id+"F1.opExtrude","SWEPT_FACE",FACE,{"disambiguationData":[OSD([sQuery(id+"F0.wireOp",EDGE,"E0")])]});Q7=makeQuery(id+"F13.opFillet","BLEND_EDGE",EDGE,{"blendedFrom":[makeQuery(id+"F8.boolean.opBoolean","MERGE",EDGE,{"derivedFrom":[makeQuery(id+"F8.opPattern","COPY",EDGE,{"derivedFrom":makeQuery(id+"F3.boolean.opBoolean","INTERSECT",EDGE,{"derivedFrom":[subQ6,subQ5]}),"instanceName":"2"}),makeQuery(id+"F8.opPattern","COPY",EDGE,{"derivedFrom":makeQuery(id+"F3.boolean.opBoolean","INTERSECT",EDGE,{"derivedFrom":[subQ6,subQ1]}),"instanceName":"3"})]}),makeQuery(id+"F12.opFillet","BLEND_FACE",FACE,{"disambiguationData":[OSD([subQ2,subQ4,subQ0]),TDD([makeQuery(id+"F8.boolean.opBoolean","MERGE",EDGE,{"derivedFrom":[makeQuery(id+"F8.opPattern","COPY",EDGE,{"derivedFrom":makeQuery(id+"F3.boolean.opBoolean","INTERSECT",EDGE,{"derivedFrom":[subQ3,subQ5]}),"instanceName":"2"}),makeQuery(id+"F8.opPattern","COPY",EDGE,{"derivedFrom":makeQuery(id+"F3.boolean.opBoolean","INTERSECT",EDGE,{"derivedFrom":[subQ3,subQ1]}),"instanceName":"3"})]})])]})],"blendedInto":[makeQuery(id+"F12.opFillet","BLEND_FACE",FACE,{"disambiguationData":[OSD([subQ2,subQ4,subQ0]),TDD([makeQuery(id+"F8.boolean.opBoolean","MERGE",EDGE,{"derivedFrom":[makeQuery(id+"F8.opPattern","COPY",EDGE,{"derivedFrom":makeQuery(id+"F3.boolean.opBoolean","INTERSECT",EDGE,{"derivedFrom":[subQ3,subQ5]}),"instanceName":"2"}),makeQuery(id+"F8.opPattern","COPY",EDGE,{"derivedFrom":makeQuery(id+"F3.boolean.opBoolean","INTERSECT",EDGE,{"derivedFrom":[subQ3,subQ1]}),"instanceName":"3"})]})])]})]});}
            var Q8;
            {var subQ0=sQuery(id+"F2.wireOp",EDGE,"E6");var subQ1=makeQuery(id+"F3.opExtrude","SWEPT_FACE",FACE,{"disambiguationData":[OSD([subQ0])]});var subQ2=sQuery(id+"F0.wireOp",EDGE,"E1.0");var subQ3=makeQuery(id+"F1.opExtrude","SWEPT_FACE",FACE,{"disambiguationData":[OSD([subQ2])]});var subQ4=sQuery(id+"F2.wireOp",EDGE,"E5");var subQ5=makeQuery(id+"F3.opExtrude","SWEPT_FACE",FACE,{"disambiguationData":[OSD([subQ4])]});var subQ6=makeQuery(id+"F1.opExtrude","SWEPT_FACE",FACE,{"disambiguationData":[OSD([sQuery(id+"F0.wireOp",EDGE,"E3")])]});Q8=makeQuery(id+"F12.opFillet","BLEND_EDGE",EDGE,{"blendedFrom":[makeQuery(id+"F8.boolean.opBoolean","MERGE",EDGE,{"derivedFrom":[makeQuery(id+"F8.opPattern","COPY",EDGE,{"derivedFrom":makeQuery(id+"F3.boolean.opBoolean","INTERSECT",EDGE,{"derivedFrom":[subQ6,subQ5]}),"instanceName":"3"}),makeQuery(id+"F8.opPattern","COPY",EDGE,{"derivedFrom":makeQuery(id+"F3.boolean.opBoolean","INTERSECT",EDGE,{"derivedFrom":[subQ6,subQ1]}),"instanceName":"4"})]}),makeQuery(id+"F11.opFillet","BLEND_FACE",FACE,{"disambiguationData":[OSD([subQ2,subQ4,subQ0]),TDD([makeQuery(id+"F8.boolean.opBoolean","MERGE",EDGE,{"derivedFrom":[makeQuery(id+"F8.opPattern","COPY",EDGE,{"derivedFrom":makeQuery(id+"F3.boolean.opBoolean","INTERSECT",EDGE,{"derivedFrom":[subQ3,subQ5]}),"instanceName":"3"}),makeQuery(id+"F8.opPattern","COPY",EDGE,{"derivedFrom":makeQuery(id+"F3.boolean.opBoolean","INTERSECT",EDGE,{"derivedFrom":[subQ3,subQ1]}),"instanceName":"4"})]})])]})],"blendedInto":[makeQuery(id+"F11.opFillet","BLEND_FACE",FACE,{"disambiguationData":[OSD([subQ2,subQ4,subQ0]),TDD([makeQuery(id+"F8.boolean.opBoolean","MERGE",EDGE,{"derivedFrom":[makeQuery(id+"F8.opPattern","COPY",EDGE,{"derivedFrom":makeQuery(id+"F3.boolean.opBoolean","INTERSECT",EDGE,{"derivedFrom":[subQ3,subQ5]}),"instanceName":"3"}),makeQuery(id+"F8.opPattern","COPY",EDGE,{"derivedFrom":makeQuery(id+"F3.boolean.opBoolean","INTERSECT",EDGE,{"derivedFrom":[subQ3,subQ1]}),"instanceName":"4"})]})])]})]});}
            var Q9;
            {var subQ0=sQuery(id+"F2.wireOp",EDGE,"E6");var subQ1=makeQuery(id+"F3.opExtrude","SWEPT_FACE",FACE,{"disambiguationData":[OSD([subQ0])]});var subQ2=sQuery(id+"F0.wireOp",EDGE,"E3");var subQ3=makeQuery(id+"F1.opExtrude","SWEPT_FACE",FACE,{"disambiguationData":[OSD([subQ2])]});var subQ4=sQuery(id+"F2.wireOp",EDGE,"E5");var subQ5=makeQuery(id+"F3.opExtrude","SWEPT_FACE",FACE,{"disambiguationData":[OSD([subQ4])]});var subQ6=makeQuery(id+"F1.opExtrude","SWEPT_FACE",FACE,{"disambiguationData":[OSD([sQuery(id+"F0.wireOp",EDGE,"E0")])]});Q9=makeQuery(id+"F13.opFillet","BLEND_EDGE",EDGE,{"blendedFrom":[makeQuery(id+"F8.boolean.opBoolean","MERGE",EDGE,{"derivedFrom":[makeQuery(id+"F8.opPattern","COPY",EDGE,{"derivedFrom":makeQuery(id+"F3.boolean.opBoolean","INTERSECT",EDGE,{"derivedFrom":[subQ6,subQ5]}),"instanceName":"3"}),makeQuery(id+"F8.opPattern","COPY",EDGE,{"derivedFrom":makeQuery(id+"F3.boolean.opBoolean","INTERSECT",EDGE,{"derivedFrom":[subQ6,subQ1]}),"instanceName":"4"})]}),makeQuery(id+"F12.opFillet","BLEND_FACE",FACE,{"disambiguationData":[OSD([subQ2,subQ4,subQ0]),TDD([makeQuery(id+"F8.boolean.opBoolean","MERGE",EDGE,{"derivedFrom":[makeQuery(id+"F8.opPattern","COPY",EDGE,{"derivedFrom":makeQuery(id+"F3.boolean.opBoolean","INTERSECT",EDGE,{"derivedFrom":[subQ3,subQ5]}),"instanceName":"3"}),makeQuery(id+"F8.opPattern","COPY",EDGE,{"derivedFrom":makeQuery(id+"F3.boolean.opBoolean","INTERSECT",EDGE,{"derivedFrom":[subQ3,subQ1]}),"instanceName":"4"})]})])]})],"blendedInto":[makeQuery(id+"F12.opFillet","BLEND_FACE",FACE,{"disambiguationData":[OSD([subQ2,subQ4,subQ0]),TDD([makeQuery(id+"F8.boolean.opBoolean","MERGE",EDGE,{"derivedFrom":[makeQuery(id+"F8.opPattern","COPY",EDGE,{"derivedFrom":makeQuery(id+"F3.boolean.opBoolean","INTERSECT",EDGE,{"derivedFrom":[subQ3,subQ5]}),"instanceName":"3"}),makeQuery(id+"F8.opPattern","COPY",EDGE,{"derivedFrom":makeQuery(id+"F3.boolean.opBoolean","INTERSECT",EDGE,{"derivedFrom":[subQ3,subQ1]}),"instanceName":"4"})]})])]})]});}
            fillet(context, id + "F14", {"entities" : qUnion([Q0, Q1, Q2, Q3, Q4, Q5, Q6, Q7, Q8, Q9]), "radius" : .75 * mm, "tangentPropagation" : true, "allowEdgeOverflow" : false});
        }
        {
            var Q0;
            Q0=makeQuery(id+"F7.opExtrude","CAP_FACE",FACE,{"disambiguationData":[OSD([sQuery(id+"F6.wireOp",EDGE,"E24")])],"isStart":false});
            var sketch = newSketch(context, id + "F15", { "sketchPlane" : qUnion([Q0])});
            skCircle(sketch, "E26", {"center": v(0, 0) * mm, "radius": 4 * mm});
            skSolve(sketch);
        }
        {
            var Q0;
            Q0 = qSketchRegion(id + "F15", true);
            extrude(context, id + "F16", {"entities" : qUnion([Q0]), "operationType" : NewBodyOperationType.REMOVE, "oppositeDirection" : true, "depth" : 1.5 * mm});
        }
    });
